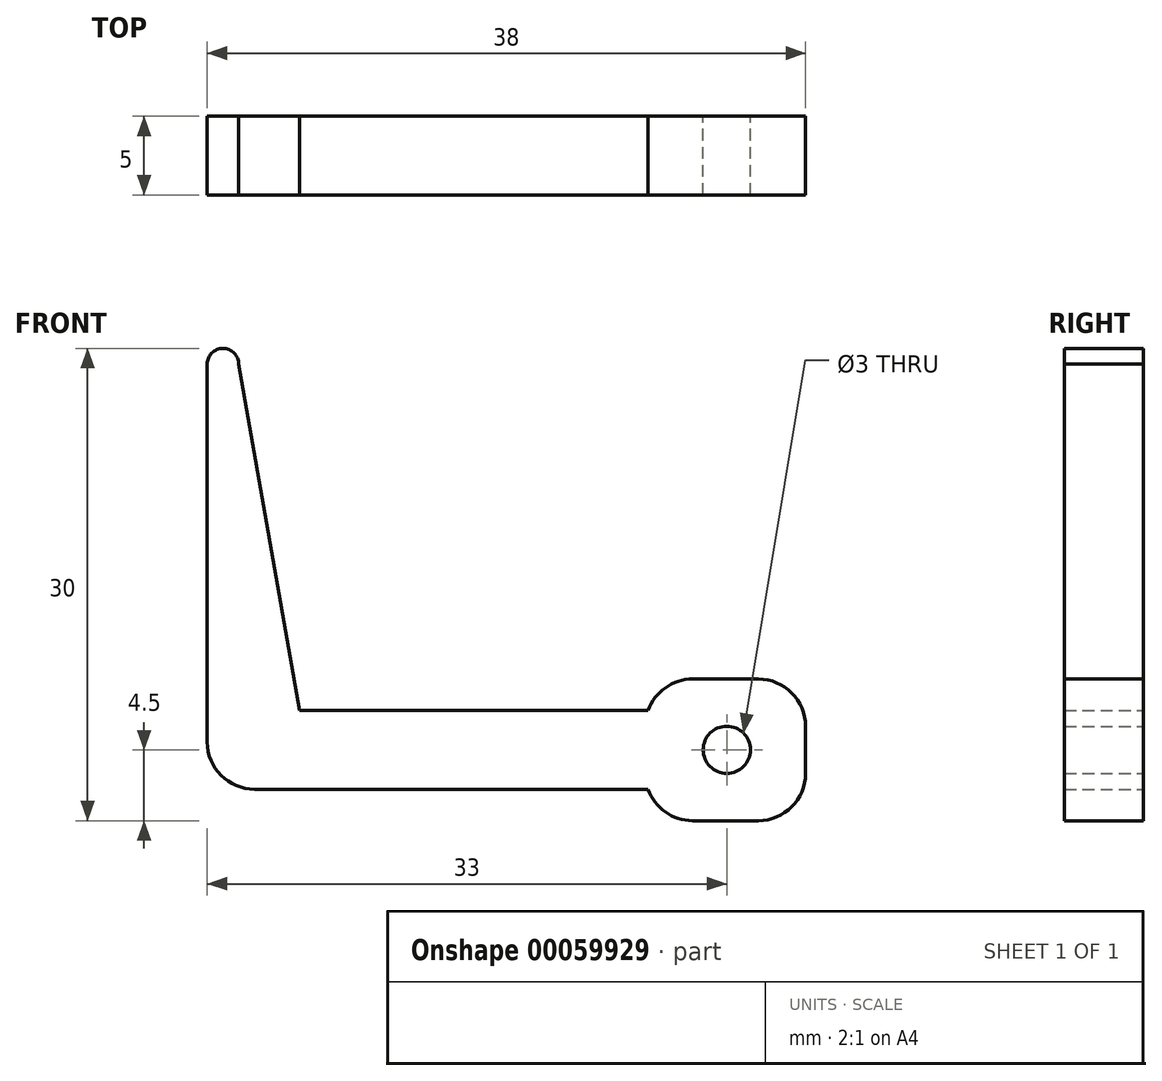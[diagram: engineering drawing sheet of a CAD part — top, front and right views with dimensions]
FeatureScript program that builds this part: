
annotation { "Feature Type Name" : "Feature", "Feature Type Description" : "" }
export const myFeature = defineFeature(function(context is Context, id is Id, definition is map)
    precondition{}
    {
        {
            var Q0;
            Q0=qCreatedBy(makeId("Front.planeOp"),FACE);
            var sketch = newSketch(context, id + "F0", { "sketchPlane" : qUnion([Q0])});
            skLineSegment(sketch, "E0", {"start": v(-10, 0) * mm, "end": v(-38, 0) * mm});
            skLineSegment(sketch, "E1", {"start": v(-32.12, 5) * mm, "end": v(-10, 5) * mm});
            skLineSegment(sketch, "E2", {"start": v(0, 5) * mm, "end": v(0, 0) * mm});
            skCircle(sketch, "E3", {"center": v(-5, 2.5) * mm, "radius": 1.5 * mm});
            skLineSegment(sketch, "E4", {"start": v(-5, 2.5) * mm, "end": v(0, 2.5) * mm, "construction": true});
            skLineSegment(sketch, "E5", {"start": v(-38, 0) * mm, "end": v(-38, 27) * mm});
            skLineSegment(sketch, "E6", {"start": v(-32.12, 5) * mm, "end": v(-36, 27) * mm});
            skArc(sketch, "E7", {"start": v(-36, 27) * mm, "mid": v(-37, 28) * mm, "end": v(-38, 27) * mm});
            skLineSegment(sketch, "E8", {"start": v(-38, 27) * mm, "end": v(-37, 27) * mm, "construction": true});
            skLineSegment(sketch, "E9", {"start": v(-37, 27) * mm, "end": v(-36, 27) * mm, "construction": true});
            skLineSegment(sketch, "E10", {"start": v(-10, 5) * mm, "end": v(-10, 7) * mm});
            skLineSegment(sketch, "E11", {"start": v(-10, 7) * mm, "end": v(0, 7) * mm});
            skLineSegment(sketch, "E12", {"start": v(0, 7) * mm, "end": v(0, 5) * mm});
            skLineSegment(sketch, "E13.MirrorCS", {"start": v(-10, 0) * mm, "end": v(-10, -2) * mm});
            skLineSegment(sketch, "E14.MirrorCS", {"start": v(-10, -2) * mm, "end": v(0, -2) * mm});
            skLineSegment(sketch, "E15.MirrorCS", {"start": v(0, -2) * mm, "end": v(0, 0) * mm});
            skSolve(sketch);
        }
        {
            var Q0;
            Q0=makeQuery(id+"F0.imprint","IMPRINT",FACE,{"disambiguationData":[TD([[makeQuery(id+"F0.imprint","IMPRINT",EDGE,{"derivedFrom":sQuery(id+"F0.wireOp",EDGE,"E0")}),-1.0]])]});
            extrude(context, id + "F1", {"entities" : qUnion([Q0]), "depth" : 5 * mm});
        }
        {
            var Q0;
            Q0=makeQuery(id+"F1.opExtrude","SWEPT_EDGE",EDGE,{"disambiguationData":[OSD([sQuery(id+"F0.wireOp",EDGE,"E11"),sQuery(id+"F0.wireOp",EDGE,"E12")])]});
            var Q1;
            Q1=makeQuery(id+"F1.opExtrude","SWEPT_EDGE",EDGE,{"disambiguationData":[OSD([sQuery(id+"F0.wireOp",EDGE,"E14.MirrorCS"),sQuery(id+"F0.wireOp",EDGE,"E15.MirrorCS")])]});
            var Q2;
            Q2=makeQuery(id+"F1.opExtrude","SWEPT_EDGE",EDGE,{"disambiguationData":[OSD([sQuery(id+"F0.wireOp",EDGE,"E10"),sQuery(id+"F0.wireOp",EDGE,"E11")])]});
            var Q3;
            Q3=makeQuery(id+"F1.opExtrude","SWEPT_EDGE",EDGE,{"disambiguationData":[OSD([sQuery(id+"F0.wireOp",EDGE,"E13.MirrorCS"),sQuery(id+"F0.wireOp",EDGE,"E14.MirrorCS")])]});
            var Q4;
            Q4=makeQuery(id+"F1.opExtrude","SWEPT_EDGE",EDGE,{"disambiguationData":[OSD([sQuery(id+"F0.wireOp",EDGE,"E0"),sQuery(id+"F0.wireOp",EDGE,"E5")])]});
            fillet(context, id + "F2", {"entities" : qUnion([Q0, Q1, Q2, Q3, Q4]), "radius" : 3 * mm, "tangentPropagation" : true, "allowEdgeOverflow" : false});
        }
    });
